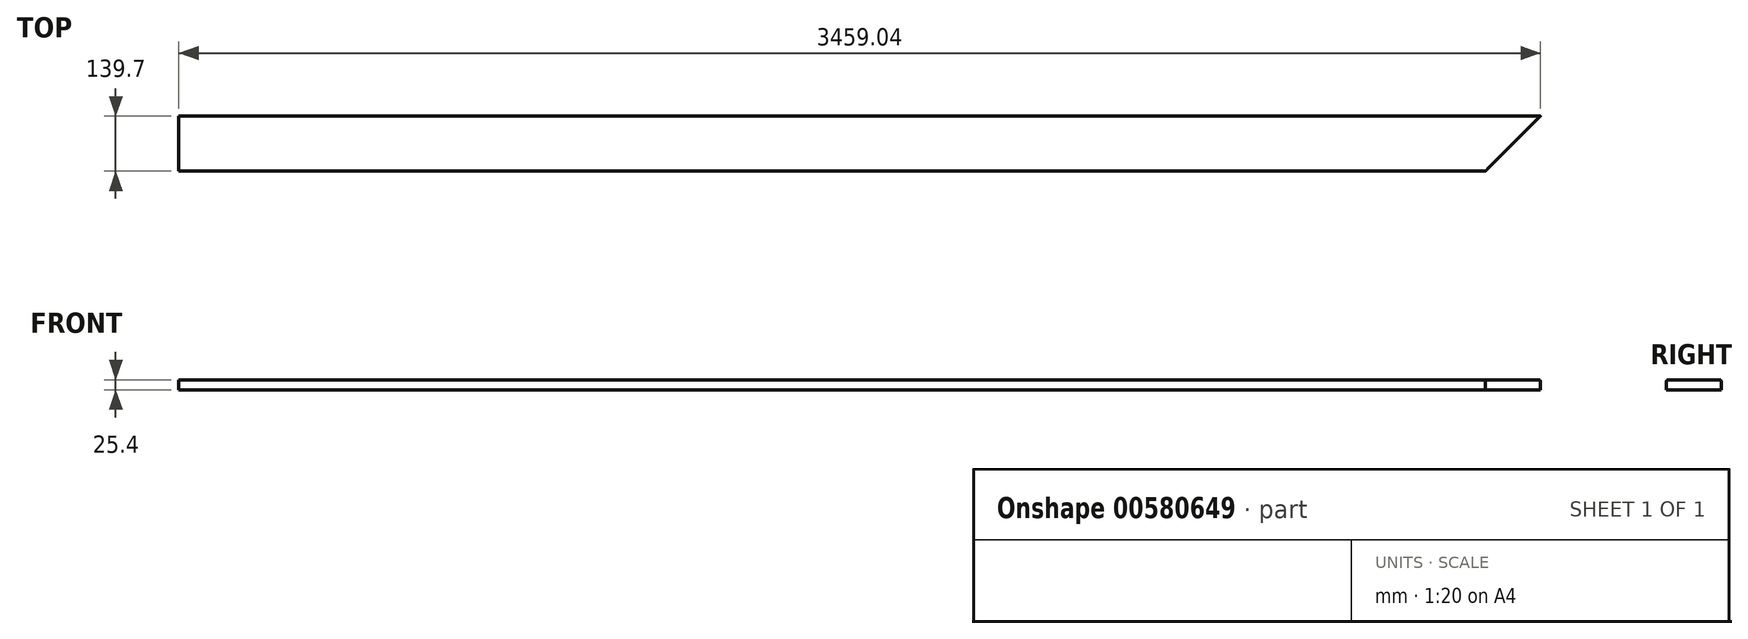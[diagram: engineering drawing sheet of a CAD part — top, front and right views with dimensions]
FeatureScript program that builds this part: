
annotation { "Feature Type Name" : "Feature", "Feature Type Description" : "" }
export const myFeature = defineFeature(function(context is Context, id is Id, definition is map)
    precondition{}
    {
        {
            var Q0;
            Q0=qCreatedBy(makeId("Top.planeOp"),FACE);
            var sketch = newSketch(context, id + "F0", { "sketchPlane" : qUnion([Q0])});
            skLineSegment(sketch, "E0.bottom", {"start": v(1589.82, -69.85) * mm, "end": v(-1729.52, -69.85) * mm});
            skLineSegment(sketch, "E0.top", {"start": v(1729.52, 69.85) * mm, "end": v(-1729.52, 69.85) * mm});
            skLineSegment(sketch, "E0.right", {"start": v(-1729.52, -69.85) * mm, "end": v(-1729.52, 69.85) * mm});
            skPoint(sketch, "E0.middle", {"position": v(0, 0) * mm});
            skLineSegment(sketch, "E1", {"start": v(1729.52, 69.85) * mm, "end": v(1589.82, -69.85) * mm});
            skSolve(sketch);
        }
        {
            var Q0;
            Q0=makeQuery(id+"F0.imprint","IMPRINT",FACE,{"disambiguationData":[TD([[makeQuery(id+"F0.imprint","IMPRINT",EDGE,{"derivedFrom":sQuery(id+"F0.wireOp",EDGE,"E0.bottom")}),-1.0]])]});
            extrude(context, id + "F1", {"entities" : qUnion([Q0]), "depth" : 25.4 * mm, "offsetDistance" : 25.4 * mm});
        }
        {
            var Q0;
            Q0=makeQuery(id+"F1.opExtrude","CAP_EDGE",EDGE,{"disambiguationData":[OSD([sQuery(id+"F0.wireOp",EDGE,"E0.top")])],"isStart":false});
            var Q1;
            Q1=makeQuery(id+"F1.opExtrude","CAP_EDGE",EDGE,{"disambiguationData":[OSD([sQuery(id+"F0.wireOp",EDGE,"E0.bottom")])],"isStart":false});
            fillet(context, id + "F2", {"entities" : qUnion([Q0, Q1]), "radius" : 5.08 * mm, "tangentPropagation" : true, "allowEdgeOverflow" : false});
        }
    });
